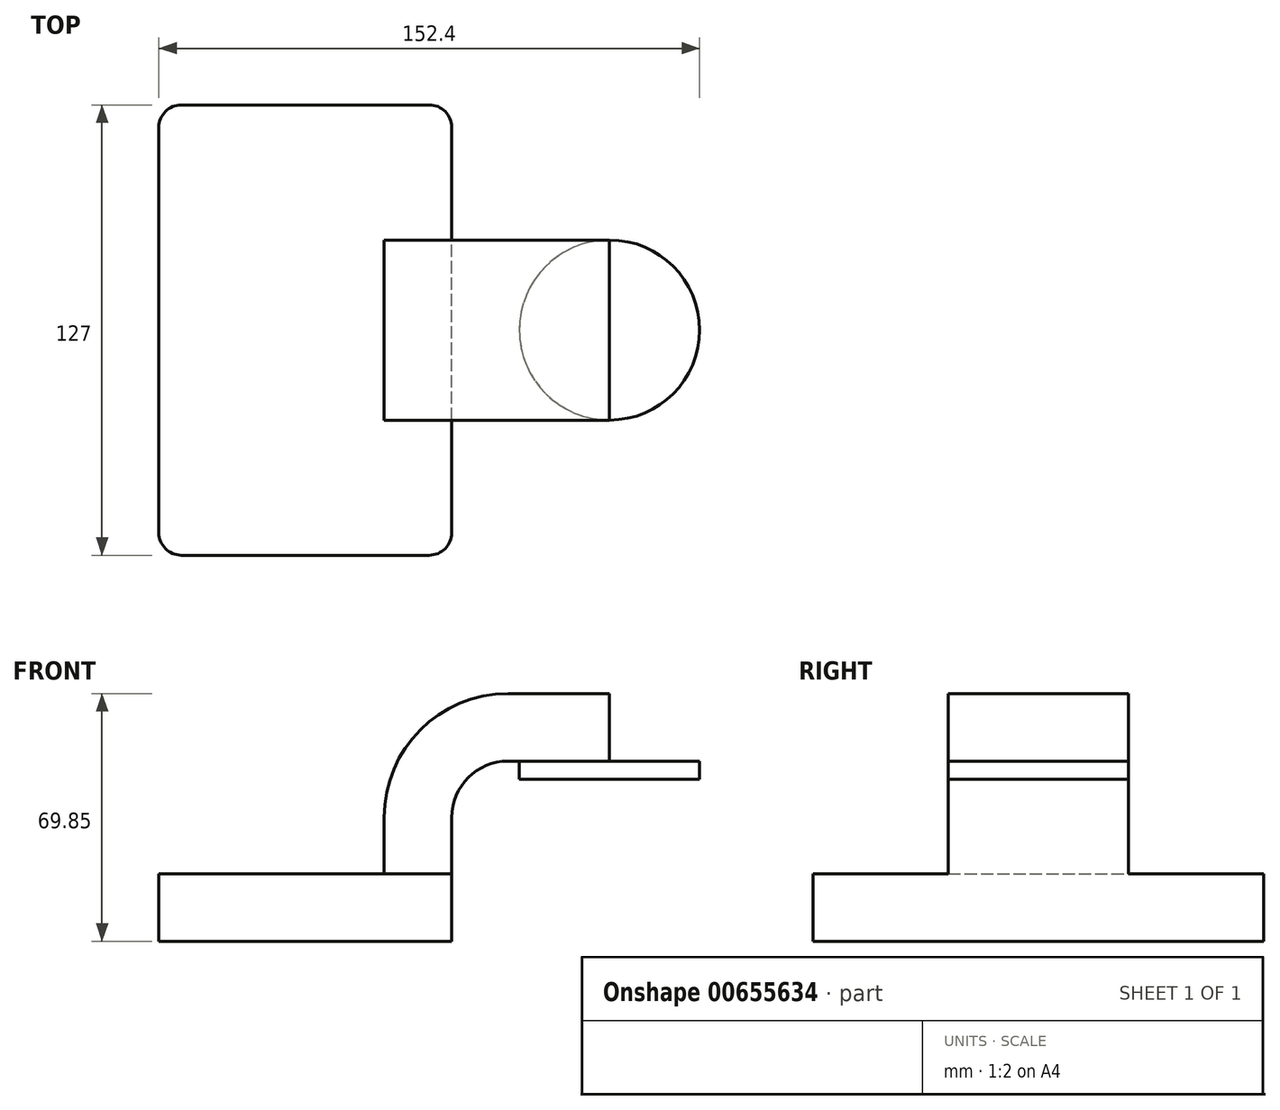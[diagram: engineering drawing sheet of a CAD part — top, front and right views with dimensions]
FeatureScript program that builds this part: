
annotation { "Feature Type Name" : "Feature", "Feature Type Description" : "" }
export const myFeature = defineFeature(function(context is Context, id is Id, definition is map)
    precondition{}
    {
        {
            var Q0;
            Q0=qCreatedBy(makeId("Front.planeOp"),FACE);
            var sketch = newSketch(context, id + "F0", { "sketchPlane" : qUnion([Q0])});
            skLineSegment(sketch, "E0.bottom", {"start": v(-41.28, -9.53) * mm, "end": v(41.27, -9.53) * mm});
            skLineSegment(sketch, "E0.top", {"start": v(-41.28, 9.52) * mm, "end": v(41.27, 9.52) * mm});
            skLineSegment(sketch, "E0.left", {"start": v(-41.28, -9.53) * mm, "end": v(-41.28, 9.52) * mm});
            skLineSegment(sketch, "E0.right", {"start": v(41.27, -9.53) * mm, "end": v(41.27, 9.52) * mm});
            skPoint(sketch, "E0.middle", {"position": v(0, 0) * mm});
            skLineSegment(sketch, "E1", {"start": v(41.27, 9.52) * mm, "end": v(41.27, 25.4) * mm});
            skArc(sketch, "E2", {"start": v(41.27, 25.4) * mm, "mid": v(45.92, 36.63) * mm, "end": v(57.15, 41.28) * mm});
            skLineSegment(sketch, "E3", {"start": v(57.15, 41.28) * mm, "end": v(85.72, 41.28) * mm});
            skLineSegment(sketch, "E4.0", {"start": v(57.15, 60.33) * mm, "end": v(85.72, 60.33) * mm});
            skArc(sketch, "E4.1", {"start": v(22.22, 25.4) * mm, "mid": v(32.45, 50.1) * mm, "end": v(57.15, 60.33) * mm});
            skLineSegment(sketch, "E4.2", {"start": v(22.22, 9.52) * mm, "end": v(22.22, 25.4) * mm});
            skFitSpline(sketch, "E5", {"points": [v(-41.28, 9.53) * mm, v(57.15, 60.33) * mm], "startDerivative": vector(3.1, 61.95) * mm, "endDerivative": vector(108.05, -0.56) * mm});
            skLineSegment(sketch, "E6", {"start": v(85.72, 60.33) * mm, "end": v(85.72, 41.28) * mm});
            skLineSegment(sketch, "E7.bottom", {"start": v(60.33, 64.77) * mm, "end": v(111.12, 64.77) * mm});
            skLineSegment(sketch, "E7.top", {"start": v(60.33, 36.2) * mm, "end": v(111.12, 36.2) * mm});
            skLineSegment(sketch, "E7.left", {"start": v(60.32, 64.77) * mm, "end": v(60.32, 36.2) * mm});
            skLineSegment(sketch, "E7.right", {"start": v(111.12, 64.77) * mm, "end": v(111.12, 36.2) * mm});
            skLineSegment(sketch, "E8", {"start": v(60.33, 36.2) * mm, "end": v(85.72, 36.2) * mm});
            skLineSegment(sketch, "E9", {"start": v(85.72, 36.2) * mm, "end": v(85.72, 64.77) * mm});
            skSolve(sketch);
        }
        {
            var Q0;
            Q0=makeQuery(id+"F0.imprint","IMPRINT",FACE,{"disambiguationData":[TD([[makeQuery(id+"F0.imprint","IMPRINT",EDGE,{"derivedFrom":sQuery(id+"F0.wireOp",EDGE,"E0.bottom")}),1.0]])]});
            extrude(context, id + "F1", {"entities" : qUnion([Q0]), "endBound" : BoundingType.SYMMETRIC, "depth" : 127 * mm, "offsetDistance" : 25.4 * mm});
        }
        {
            var Q0;
            {var subQ1=sQuery(id+"F0.wireOp",EDGE,"E1");Q0=makeQuery(id+"F0.imprint","IMPRINT",FACE,{"disambiguationData":[TD([[makeQuery(id+"F0.imprint","IMPRINT",EDGE,{"derivedFrom":subQ1}),1.0]])]});}
            extrude(context, id + "F2", {"entities" : qUnion([Q0]), "operationType" : NewBodyOperationType.ADD, "endBound" : BoundingType.SYMMETRIC, "depth" : 50.8 * mm, "offsetDistance" : 25.4 * mm});
        }
        {
            var Q0;
            Q0=makeQuery(id+"F0.imprint","IMPRINT",FACE,{"disambiguationData":[TD([[makeQuery(id+"F0.imprint","IMPRINT",EDGE,{"derivedFrom":sQuery(id+"F0.wireOp",EDGE,"E4.1")}),1.0]])]});
            extrude(context, id + "F3", {"entities" : qUnion([Q0]), "operationType" : NewBodyOperationType.ADD, "endBound" : BoundingType.SYMMETRIC, "depth" : 15.88 * mm, "offsetDistance" : 25.4 * mm});
        }
        {
            var Q0;
            {var subQ0=sQuery(id+"F0.wireOp",EDGE,"E9");var subQ1=sQuery(id+"F0.wireOp",EDGE,"E3");var subQ2=makeQuery(id+"F0.imprint","INTERSECT",VERTEX,{"derivedFrom":[subQ1,subQ0]});Q0=makeQuery(id+"F0.imprint","IMPRINT",FACE,{"disambiguationData":[TD([[makeQuery(id+"F0.imprint","IMPRINT",EDGE,{"disambiguationData":[TD([[subQ2,1.0]])],"derivedFrom":subQ1}),1.0]])]});}
            extrude(context, id + "F4", {"entities" : qUnion([Q0]), "operationType" : NewBodyOperationType.ADD, "endBound" : BoundingType.SYMMETRIC, "depth" : 50.8 * mm, "offsetDistance" : 25.4 * mm});
        }
        {
            var Q0;
            {var subQ2=sQuery(id+"F0.wireOp",EDGE,"E7.top");Q0=makeQuery(id+"F0.imprint","IMPRINT",FACE,{"disambiguationData":[TD([[makeQuery(id+"F0.imprint","IMPRINT",EDGE,{"derivedFrom":subQ2}),1.0]])]});}
            var Q1;
            Q1=sQuery(id+"F0.wireOp",EDGE,"E6");
            revolve(context, id + "F5", {"operationType" : NewBodyOperationType.ADD, "entities" : qUnion([Q0]), "axis" : qUnion([Q1]), "revolveType" : RevolveType.FULL});
        }
        {
            var Q0;
            Q0=makeQuery(id+"F1.opExtrude","CAP_EDGE",EDGE,{"disambiguationData":[OSD([sQuery(id+"F0.wireOp",EDGE,"E0.right")])],"isStart":false});
            var Q1;
            Q1=makeQuery(id+"F1.opExtrude","CAP_EDGE",EDGE,{"disambiguationData":[OSD([sQuery(id+"F0.wireOp",EDGE,"E0.left")])],"isStart":false});
            var Q2;
            Q2=makeQuery(id+"F1.opExtrude","CAP_EDGE",EDGE,{"disambiguationData":[OSD([sQuery(id+"F0.wireOp",EDGE,"E0.right")])],"isStart":true});
            var Q3;
            Q3=makeQuery(id+"F1.opExtrude","CAP_EDGE",EDGE,{"disambiguationData":[OSD([sQuery(id+"F0.wireOp",EDGE,"E0.left")])],"isStart":true});
            fillet(context, id + "F6", {"entities" : qUnion([Q0, Q1, Q2, Q3]), "radius" : 6.35 * mm, "tangentPropagation" : true, "allowEdgeOverflow" : false});
        }
    });
